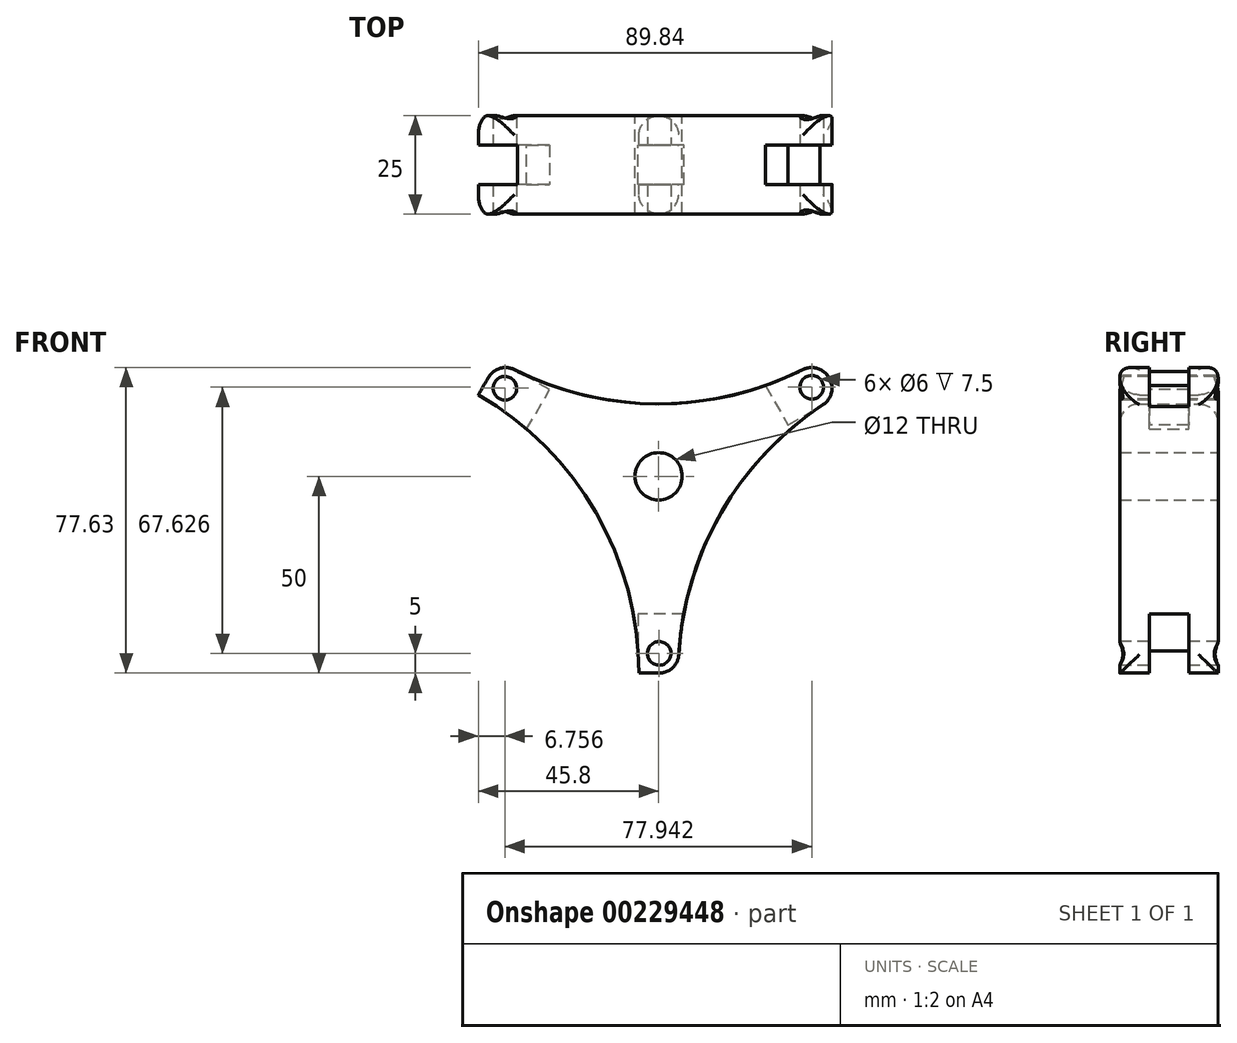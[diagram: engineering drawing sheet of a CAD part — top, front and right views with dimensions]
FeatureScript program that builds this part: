
annotation { "Feature Type Name" : "Feature", "Feature Type Description" : "" }
export const myFeature = defineFeature(function(context is Context, id is Id, definition is map)
    precondition{}
    {
        {
            var Q0;
            Q0=qCreatedBy(makeId("Front.planeOp"),FACE);
            var sketch = newSketch(context, id + "F0", { "sketchPlane" : qUnion([Q0])});
            skLineSegment(sketch, "E0", {"start": v(-43.3, 25) * mm, "end": v(0, 0) * mm, "construction": true});
            skLineSegment(sketch, "E1", {"start": v(0, 0) * mm, "end": v(0, -50) * mm, "construction": true});
            skLineSegment(sketch, "E2", {"start": v(0, 0) * mm, "end": v(43.3, 25) * mm, "construction": true});
            skLineSegment(sketch, "E3", {"start": v(-5, -50) * mm, "end": v(5, -50) * mm});
            skLineSegment(sketch, "E4.1.0", {"start": v(-40.8, 29.33) * mm, "end": v(-45.8, 20.67) * mm});
            skLineSegment(sketch, "E4.2.0", {"start": v(45.8, 20.67) * mm, "end": v(40.8, 29.33) * mm});
            skPoint(sketch, "E4.center", {"position": v(0, 0) * mm});
            skLineSegment(sketch, "E4.anchor1", {"start": v(0, 0) * mm, "end": v(-5, -50) * mm, "construction": true});
            skLineSegment(sketch, "E4.anchor2", {"start": v(0, 0) * mm, "end": v(45.8, 20.67) * mm, "construction": true});
            skArc(sketch, "E5", {"start": v(-5, -50) * mm, "mid": v(-15.93, -9.2) * mm, "end": v(-45.8, 20.67) * mm});
            skArc(sketch, "E6.1.0", {"start": v(45.8, 20.67) * mm, "mid": v(15.93, -9.2) * mm, "end": v(5, -50) * mm});
            skArc(sketch, "E6.2.0", {"start": v(-40.8, 29.33) * mm, "mid": v(0, 18.4) * mm, "end": v(40.8, 29.33) * mm});
            skCircle(sketch, "E7", {"center": v(0, 0) * mm, "radius": 6 * mm});
            skSolve(sketch);
        }
        {
            var Q0;
            Q0=makeQuery(id+"F0.imprint","IMPRINT",FACE,{"disambiguationData":[TD([[makeQuery(id+"F0.imprint","IMPRINT",EDGE,{"derivedFrom":sQuery(id+"F0.wireOp",EDGE,"E3")}),1.0]])]});
            extrude(context, id + "F1", {"entities" : qUnion([Q0]), "depth" : 25 * mm});
        }
        {
            var Q0;
            Q0=makeQuery(id+"F1.opExtrude","CAP_EDGE",EDGE,{"disambiguationData":[OSD([sQuery(id+"F0.wireOp",EDGE,"E6.2.0")])],"isStart":false});
            var Q1;
            Q1=makeQuery(id+"F1.opExtrude","SWEPT_FACE",FACE,{"disambiguationData":[OSD([sQuery(id+"F0.wireOp",EDGE,"E6.2.0")])]});
            var Q2;
            Q2=makeQuery(id+"F1.opExtrude","CAP_EDGE",EDGE,{"disambiguationData":[OSD([sQuery(id+"F0.wireOp",EDGE,"E5")])],"isStart":false});
            var Q3;
            Q3=makeQuery(id+"F1.opExtrude","CAP_EDGE",EDGE,{"disambiguationData":[OSD([sQuery(id+"F0.wireOp",EDGE,"E6.1.0")])],"isStart":false});
            var Q4;
            Q4=makeQuery(id+"F1.opExtrude","SWEPT_FACE",FACE,{"disambiguationData":[OSD([sQuery(id+"F0.wireOp",EDGE,"E6.1.0")])]});
            var Q5;
            Q5=makeQuery(id+"F1.opExtrude","CAP_EDGE",EDGE,{"disambiguationData":[OSD([sQuery(id+"F0.wireOp",EDGE,"E5")])],"isStart":true});
            fillet(context, id + "F2", {"entities" : qUnion([Q0, Q1, Q2, Q3, Q4, Q5]), "radius" : 5 * mm, "tangentPropagation" : true, "allowEdgeOverflow" : false});
        }
        {
            var Q0;
            Q0=qCreatedBy(makeId("Front.planeOp"),FACE);
            cPlane(context, id + "F3", {"entities" : qUnion([Q0]), "cplaneType" : CPlaneType.OFFSET, "offset" : 12.5 * mm, "width" : 150 * mm, "height" : 150 * mm});
        }
        {
            var Q0;
            Q0=qCreatedBy(id+"F3.planeOp",FACE);
            var sketch = newSketch(context, id + "F4", { "sketchPlane" : qUnion([Q0])});
            skLineSegment(sketch, "E8", {"start": v(26.9, 23.4) * mm, "end": v(32.9, 13) * mm});
            skLineSegment(sketch, "E9", {"start": v(32.9, 13) * mm, "end": v(56.3, 26.5) * mm});
            skLineSegment(sketch, "E10", {"start": v(56.3, 26.5) * mm, "end": v(50.3, 36.9) * mm});
            skLineSegment(sketch, "E11", {"start": v(43.3, 25) * mm, "end": v(60.06, 34.67) * mm, "construction": true});
            skLineSegment(sketch, "E12", {"start": v(26.9, 23.4) * mm, "end": v(50.3, 36.9) * mm});
            skLineSegment(sketch, "E13.1.0", {"start": v(-33.71, 11.6) * mm, "end": v(-57.1, 25.1) * mm});
            skLineSegment(sketch, "E13.1.1", {"start": v(-33.71, 11.6) * mm, "end": v(-27.71, 22) * mm});
            skLineSegment(sketch, "E13.1.2", {"start": v(-27.71, 22) * mm, "end": v(-51.1, 35.5) * mm});
            skLineSegment(sketch, "E13.1.3", {"start": v(-51.1, 35.5) * mm, "end": v(-57.1, 25.1) * mm});
            skLineSegment(sketch, "E13.2.0", {"start": v(6.8, -35) * mm, "end": v(6.8, -62) * mm});
            skLineSegment(sketch, "E13.2.1", {"start": v(6.8, -35) * mm, "end": v(-5.2, -35) * mm});
            skLineSegment(sketch, "E13.2.2", {"start": v(-5.2, -35) * mm, "end": v(-5.2, -62) * mm});
            skLineSegment(sketch, "E13.2.3", {"start": v(-5.2, -62) * mm, "end": v(6.8, -62) * mm});
            skPoint(sketch, "E13.center", {"position": v(0, 0) * mm});
            skSolve(sketch);
        }
        {
            var Q0;
            Q0=makeQuery(id+"F4.imprint","IMPRINT",FACE,{"disambiguationData":[TD([[makeQuery(id+"F4.imprint","IMPRINT",EDGE,{"derivedFrom":sQuery(id+"F4.wireOp",EDGE,"E8")}),1.0]])]});
            var Q1;
            Q1=makeQuery(id+"F4.imprint","IMPRINT",FACE,{"disambiguationData":[TD([[makeQuery(id+"F4.imprint","IMPRINT",EDGE,{"derivedFrom":sQuery(id+"F4.wireOp",EDGE,"E13.1.0")}),-1.0]])]});
            var Q2;
            Q2=makeQuery(id+"F4.imprint","IMPRINT",FACE,{"disambiguationData":[TD([[makeQuery(id+"F4.imprint","IMPRINT",EDGE,{"derivedFrom":sQuery(id+"F4.wireOp",EDGE,"E13.2.0")}),-1.0]])]});
            extrude(context, id + "F5", {"entities" : qUnion([Q0, Q1, Q2]), "operationType" : NewBodyOperationType.REMOVE, "endBound" : BoundingType.SYMMETRIC, "oppositeDirection" : true, "depth" : 10 * mm});
        }
        {
            var Q0;
            Q0=qCreatedBy(id+"F3.planeOp",FACE);
            var sketch = newSketch(context, id + "F6", { "sketchPlane" : qUnion([Q0])});
            skArc(sketch, "E14.0", {"start": v(36.65, 27.1) * mm, "mid": v(40.33, 27.42) * mm, "end": v(43.23, 25.13) * mm, "construction": true});
            skArc(sketch, "E15.0", {"start": v(-43.23, 25.13) * mm, "mid": v(-40.33, 27.42) * mm, "end": v(-36.65, 27.1) * mm, "construction": true});
            skArc(sketch, "E16.0", {"start": v(5.14, -45.29) * mm, "mid": v(3.58, -48.64) * mm, "end": v(0.14, -50) * mm, "construction": true});
            skCircle(sketch, "E17", {"center": v(38.9, 22.63) * mm, "radius": 3 * mm});
            skCircle(sketch, "E18.1.0", {"center": v(-39.04, 22.37) * mm, "radius": 3 * mm});
            skCircle(sketch, "E18.2.0", {"center": v(0.14, -45) * mm, "radius": 3 * mm});
            skPoint(sketch, "E18.center", {"position": v(0, 0) * mm});
            skSolve(sketch);
        }
        {
            var Q0;
            Q0=makeQuery(id+"F6.imprint","IMPRINT",FACE,{"disambiguationData":[TD([[makeQuery(id+"F6.imprint","IMPRINT",EDGE,{"derivedFrom":sQuery(id+"F6.wireOp",EDGE,"E17")}),1.0]])]});
            var Q1;
            Q1=makeQuery(id+"F6.imprint","IMPRINT",FACE,{"disambiguationData":[TD([[makeQuery(id+"F6.imprint","IMPRINT",EDGE,{"derivedFrom":sQuery(id+"F6.wireOp",EDGE,"E18.2.0")}),1.0]])]});
            var Q2;
            Q2=makeQuery(id+"F6.imprint","IMPRINT",FACE,{"disambiguationData":[TD([[makeQuery(id+"F6.imprint","IMPRINT",EDGE,{"derivedFrom":sQuery(id+"F6.wireOp",EDGE,"E18.1.0")}),1.0]])]});
            extrude(context, id + "F7", {"entities" : qUnion([Q0, Q1, Q2]), "operationType" : NewBodyOperationType.REMOVE, "endBound" : BoundingType.SYMMETRIC, "oppositeDirection" : true, "depth" : 25 * mm});
        }
    });
